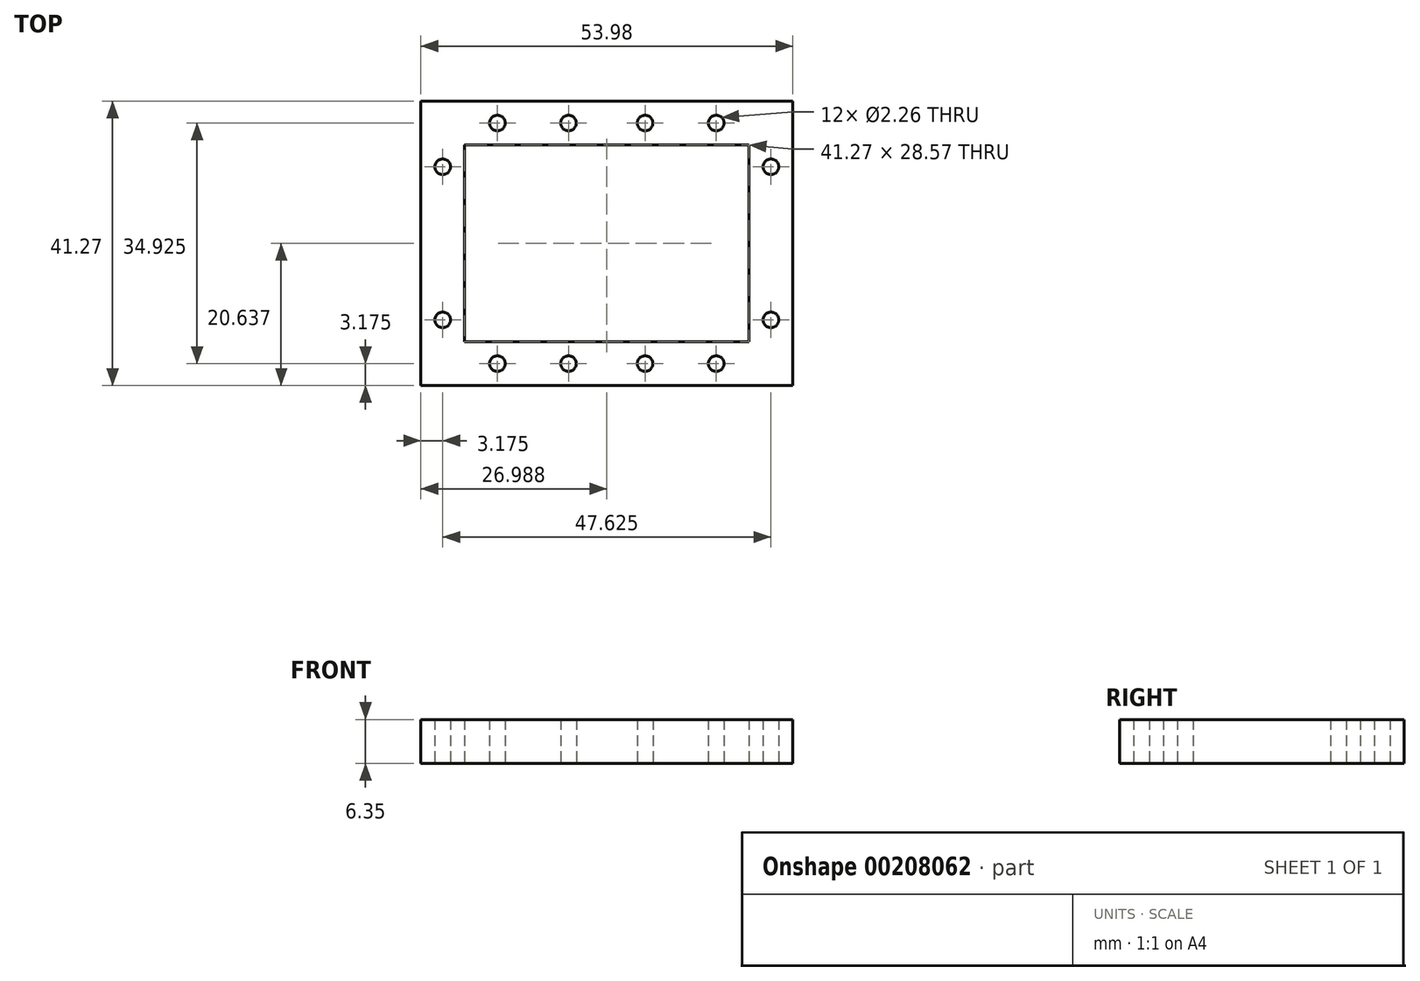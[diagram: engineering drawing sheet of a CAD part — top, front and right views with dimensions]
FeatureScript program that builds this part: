
annotation { "Feature Type Name" : "Feature", "Feature Type Description" : "" }
export const myFeature = defineFeature(function(context is Context, id is Id, definition is map)
    precondition{}
    {
        {
            var Q0;
            Q0=qCreatedBy(makeId("Top.planeOp"),FACE);
            var sketch = newSketch(context, id + "F0", { "sketchPlane" : qUnion([Q0])});
            skLineSegment(sketch, "E0", {"start": v(0, 0) * mm, "end": v(53.98, 0) * mm});
            skLineSegment(sketch, "E1", {"start": v(53.98, 0) * mm, "end": v(53.98, 41.27) * mm});
            skLineSegment(sketch, "E2", {"start": v(53.97, 41.27) * mm, "end": v(0, 41.27) * mm});
            skLineSegment(sketch, "E3", {"start": v(0, 41.27) * mm, "end": v(0, 0) * mm});
            skPoint(sketch, "E4", {"position": v(26.99, 20.64) * mm});
            skPoint(sketch, "E5", {"position": v(11.11, 3.18) * mm});
            skPoint(sketch, "E6", {"position": v(21.43, 3.18) * mm});
            skPoint(sketch, "E7", {"position": v(32.54, 3.18) * mm});
            skPoint(sketch, "E8", {"position": v(42.86, 3.18) * mm});
            skLineSegment(sketch, "E9", {"start": v(11.11, 3.18) * mm, "end": v(0, 3.18) * mm});
            skLineSegment(sketch, "E10", {"start": v(42.86, 3.18) * mm, "end": v(53.98, 3.18) * mm});
            skLineSegment(sketch, "E11", {"start": v(11.11, 3.18) * mm, "end": v(21.43, 3.18) * mm});
            skLineSegment(sketch, "E12", {"start": v(42.86, 3.18) * mm, "end": v(32.54, 3.18) * mm});
            skPoint(sketch, "E13", {"position": v(11.11, 38.1) * mm});
            skPoint(sketch, "E14", {"position": v(21.43, 38.1) * mm});
            skPoint(sketch, "E15", {"position": v(32.54, 38.1) * mm});
            skPoint(sketch, "E16", {"position": v(42.86, 38.1) * mm});
            skLineSegment(sketch, "E17", {"start": v(11.11, 38.1) * mm, "end": v(0, 38.1) * mm});
            skLineSegment(sketch, "E18", {"start": v(42.86, 38.1) * mm, "end": v(53.97, 38.1) * mm});
            skLineSegment(sketch, "E19", {"start": v(11.11, 38.1) * mm, "end": v(21.43, 38.1) * mm});
            skLineSegment(sketch, "E20", {"start": v(42.86, 38.1) * mm, "end": v(32.54, 38.1) * mm});
            skPoint(sketch, "E21", {"position": v(3.18, 9.53) * mm});
            skPoint(sketch, "E22", {"position": v(3.18, 31.75) * mm});
            skLineSegment(sketch, "E23", {"start": v(3.18, 9.53) * mm, "end": v(3.18, 0) * mm});
            skLineSegment(sketch, "E24", {"start": v(3.18, 31.75) * mm, "end": v(3.18, 41.28) * mm});
            skPoint(sketch, "E25", {"position": v(50.8, 9.53) * mm});
            skPoint(sketch, "E26", {"position": v(50.8, 31.75) * mm});
            skLineSegment(sketch, "E27", {"start": v(50.8, 9.53) * mm, "end": v(50.8, 0) * mm});
            skLineSegment(sketch, "E28", {"start": v(50.8, 31.75) * mm, "end": v(50.8, 41.28) * mm});
            skSolve(sketch);
        }
        {
            var Q0;
            Q0 = qSketchRegion(id + "F0", true);
            extrude(context, id + "F1", {"entities" : qUnion([Q0]), "depth" : 6.35 * mm});
        }
        {
            var Q0;
            Q0=makeQuery(id+"F1.opExtrude","CAP_FACE",FACE,{"disambiguationData":[OSD([sQuery(id+"F0.wireOp",EDGE,"E0"),sQuery(id+"F0.wireOp",EDGE,"E1"),sQuery(id+"F0.wireOp",EDGE,"E2"),sQuery(id+"F0.wireOp",EDGE,"E3")])],"isStart":true});
            var sketch = newSketch(context, id + "F2", { "sketchPlane" : qUnion([Q0])});
            skLineSegment(sketch, "E29", {"start": v(6.35, -6.35) * mm, "end": v(47.62, -6.35) * mm});
            skLineSegment(sketch, "E30", {"start": v(47.62, -6.35) * mm, "end": v(47.62, -34.93) * mm});
            skLineSegment(sketch, "E31", {"start": v(47.62, -34.93) * mm, "end": v(6.35, -34.93) * mm});
            skLineSegment(sketch, "E32", {"start": v(6.35, -34.93) * mm, "end": v(6.35, -6.35) * mm});
            skPoint(sketch, "E33", {"position": v(26.99, -20.64) * mm});
            skSolve(sketch);
        }
        {
            var Q0;
            Q0 = qSketchRegion(id + "F2", true);
            extrude(context, id + "F3", {"entities" : qUnion([Q0]), "operationType" : NewBodyOperationType.REMOVE, "endBound" : BoundingType.UP_TO_NEXT, "oppositeDirection" : true, "depth" : 25.4 * mm});
        }
        {
            var Q0;
            Q0=sQuery(id+"F0.wireOp",VERTEX,"E5");
            var Q1;
            Q1=makeQuery(id+"F1.opExtrude","SWEPT_BODY",BODY,{"disambiguationData":[OSD([sQuery(id+"F0.wireOp",EDGE,"E0"),sQuery(id+"F0.wireOp",EDGE,"E1"),sQuery(id+"F0.wireOp",EDGE,"E2"),sQuery(id+"F0.wireOp",EDGE,"E3")])]});
            hole(context, id + "F4", {"style" : HoleStyle.SIMPLE, "endStyle" : HoleEndStyle.THROUGH, "oppositeDirection" : true, "standardTappedOrClearance" : lookupTablePath({ "standard" : "ANSI", "engagement" : "75%", "pitch" : "40 tpi", "size" : "#4", "type" : "Tapped" }), "standardBlindInLast" : lookupTablePath({ "standard" : "ANSI", "engagement" : "75%", "pitch" : "40 tpi", "size" : "#4", "type" : "Tapped" }), "holeDiameter" : 2.26 * mm, "showTappedDepth" : true, "tappedDepth" : 12.7 * mm, "tapClearance" : 3, "locations" : qUnion([Q0]), "scope" : qUnion([Q1]), "majorDiameter" : 2.84 * mm});
        }
        {
            var Q0;
            Q0=sQuery(id+"F0.wireOp",VERTEX,"E6");
            var Q1;
            Q1=makeQuery(id+"F1.opExtrude","SWEPT_BODY",BODY,{"disambiguationData":[OSD([sQuery(id+"F0.wireOp",EDGE,"E0"),sQuery(id+"F0.wireOp",EDGE,"E1"),sQuery(id+"F0.wireOp",EDGE,"E2"),sQuery(id+"F0.wireOp",EDGE,"E3")])]});
            hole(context, id + "F5", {"style" : HoleStyle.SIMPLE, "endStyle" : HoleEndStyle.THROUGH, "oppositeDirection" : true, "standardTappedOrClearance" : lookupTablePath({ "standard" : "ANSI", "engagement" : "75%", "pitch" : "40 tpi", "size" : "#4", "type" : "Tapped" }), "standardBlindInLast" : lookupTablePath({ "standard" : "ANSI", "engagement" : "75%", "pitch" : "40 tpi", "size" : "#4", "type" : "Tapped" }), "holeDiameter" : 2.26 * mm, "showTappedDepth" : true, "tappedDepth" : 12.7 * mm, "tapClearance" : 3, "locations" : qUnion([Q0]), "scope" : qUnion([Q1]), "majorDiameter" : 2.84 * mm});
        }
        {
            var Q0;
            Q0=sQuery(id+"F0.wireOp",VERTEX,"E7");
            var Q1;
            Q1=makeQuery(id+"F1.opExtrude","SWEPT_BODY",BODY,{"disambiguationData":[OSD([sQuery(id+"F0.wireOp",EDGE,"E0"),sQuery(id+"F0.wireOp",EDGE,"E1"),sQuery(id+"F0.wireOp",EDGE,"E2"),sQuery(id+"F0.wireOp",EDGE,"E3")])]});
            hole(context, id + "F6", {"style" : HoleStyle.SIMPLE, "endStyle" : HoleEndStyle.THROUGH, "oppositeDirection" : true, "standardTappedOrClearance" : lookupTablePath({ "standard" : "ANSI", "engagement" : "75%", "pitch" : "40 tpi", "size" : "#4", "type" : "Tapped" }), "standardBlindInLast" : lookupTablePath({ "standard" : "ANSI", "engagement" : "75%", "pitch" : "40 tpi", "size" : "#4", "type" : "Tapped" }), "holeDiameter" : 2.26 * mm, "showTappedDepth" : true, "tappedDepth" : 12.7 * mm, "tapClearance" : 3, "locations" : qUnion([Q0]), "scope" : qUnion([Q1]), "majorDiameter" : 2.84 * mm});
        }
        {
            var Q0;
            Q0=sQuery(id+"F0.wireOp",VERTEX,"E8");
            var Q1;
            Q1=makeQuery(id+"F1.opExtrude","SWEPT_BODY",BODY,{"disambiguationData":[OSD([sQuery(id+"F0.wireOp",EDGE,"E0"),sQuery(id+"F0.wireOp",EDGE,"E1"),sQuery(id+"F0.wireOp",EDGE,"E2"),sQuery(id+"F0.wireOp",EDGE,"E3")])]});
            hole(context, id + "F7", {"style" : HoleStyle.SIMPLE, "endStyle" : HoleEndStyle.THROUGH, "oppositeDirection" : true, "standardTappedOrClearance" : lookupTablePath({ "standard" : "ANSI", "engagement" : "75%", "pitch" : "40 tpi", "size" : "#4", "type" : "Tapped" }), "standardBlindInLast" : lookupTablePath({ "standard" : "ANSI", "engagement" : "75%", "pitch" : "40 tpi", "size" : "#4", "type" : "Tapped" }), "holeDiameter" : 2.26 * mm, "showTappedDepth" : true, "tappedDepth" : 12.7 * mm, "tapClearance" : 3, "locations" : qUnion([Q0]), "scope" : qUnion([Q1]), "majorDiameter" : 2.84 * mm});
        }
        {
            var Q0;
            Q0=sQuery(id+"F0.wireOp",VERTEX,"E13");
            var Q1;
            Q1=makeQuery(id+"F1.opExtrude","SWEPT_BODY",BODY,{"disambiguationData":[OSD([sQuery(id+"F0.wireOp",EDGE,"E0"),sQuery(id+"F0.wireOp",EDGE,"E1"),sQuery(id+"F0.wireOp",EDGE,"E2"),sQuery(id+"F0.wireOp",EDGE,"E3")])]});
            hole(context, id + "F8", {"style" : HoleStyle.SIMPLE, "endStyle" : HoleEndStyle.THROUGH, "oppositeDirection" : true, "standardTappedOrClearance" : lookupTablePath({ "standard" : "ANSI", "engagement" : "75%", "pitch" : "40 tpi", "size" : "#4", "type" : "Tapped" }), "standardBlindInLast" : lookupTablePath({ "standard" : "ANSI", "engagement" : "75%", "pitch" : "40 tpi", "size" : "#4", "type" : "Tapped" }), "holeDiameter" : 2.26 * mm, "showTappedDepth" : true, "tappedDepth" : 12.7 * mm, "tapClearance" : 3, "locations" : qUnion([Q0]), "scope" : qUnion([Q1]), "majorDiameter" : 2.84 * mm});
        }
        {
            var Q0;
            Q0=sQuery(id+"F0.wireOp",VERTEX,"E14");
            var Q1;
            Q1=makeQuery(id+"F1.opExtrude","SWEPT_BODY",BODY,{"disambiguationData":[OSD([sQuery(id+"F0.wireOp",EDGE,"E0"),sQuery(id+"F0.wireOp",EDGE,"E1"),sQuery(id+"F0.wireOp",EDGE,"E2"),sQuery(id+"F0.wireOp",EDGE,"E3")])]});
            hole(context, id + "F9", {"style" : HoleStyle.SIMPLE, "endStyle" : HoleEndStyle.THROUGH, "oppositeDirection" : true, "standardTappedOrClearance" : lookupTablePath({ "standard" : "ANSI", "engagement" : "75%", "pitch" : "40 tpi", "size" : "#4", "type" : "Tapped" }), "standardBlindInLast" : lookupTablePath({ "standard" : "ANSI", "engagement" : "75%", "pitch" : "40 tpi", "size" : "#4", "type" : "Tapped" }), "holeDiameter" : 2.26 * mm, "showTappedDepth" : true, "tappedDepth" : 12.7 * mm, "tapClearance" : 3, "locations" : qUnion([Q0]), "scope" : qUnion([Q1]), "majorDiameter" : 2.84 * mm});
        }
        {
            var Q0;
            Q0=sQuery(id+"F0.wireOp",VERTEX,"E15");
            var Q1;
            Q1=makeQuery(id+"F1.opExtrude","SWEPT_BODY",BODY,{"disambiguationData":[OSD([sQuery(id+"F0.wireOp",EDGE,"E0"),sQuery(id+"F0.wireOp",EDGE,"E1"),sQuery(id+"F0.wireOp",EDGE,"E2"),sQuery(id+"F0.wireOp",EDGE,"E3")])]});
            hole(context, id + "F10", {"style" : HoleStyle.SIMPLE, "endStyle" : HoleEndStyle.THROUGH, "oppositeDirection" : true, "standardTappedOrClearance" : lookupTablePath({ "standard" : "ANSI", "engagement" : "75%", "pitch" : "40 tpi", "size" : "#4", "type" : "Tapped" }), "standardBlindInLast" : lookupTablePath({ "standard" : "ANSI", "engagement" : "75%", "pitch" : "40 tpi", "size" : "#4", "type" : "Tapped" }), "holeDiameter" : 2.26 * mm, "showTappedDepth" : true, "tappedDepth" : 12.7 * mm, "tapClearance" : 3, "locations" : qUnion([Q0]), "scope" : qUnion([Q1]), "majorDiameter" : 2.84 * mm});
        }
        {
            var Q0;
            Q0=sQuery(id+"F0.wireOp",VERTEX,"E16");
            var Q1;
            Q1=makeQuery(id+"F1.opExtrude","SWEPT_BODY",BODY,{"disambiguationData":[OSD([sQuery(id+"F0.wireOp",EDGE,"E0"),sQuery(id+"F0.wireOp",EDGE,"E1"),sQuery(id+"F0.wireOp",EDGE,"E2"),sQuery(id+"F0.wireOp",EDGE,"E3")])]});
            hole(context, id + "F11", {"style" : HoleStyle.SIMPLE, "endStyle" : HoleEndStyle.THROUGH, "oppositeDirection" : true, "standardTappedOrClearance" : lookupTablePath({ "standard" : "ANSI", "engagement" : "75%", "pitch" : "40 tpi", "size" : "#4", "type" : "Tapped" }), "standardBlindInLast" : lookupTablePath({ "standard" : "ANSI", "engagement" : "75%", "pitch" : "40 tpi", "size" : "#4", "type" : "Tapped" }), "holeDiameter" : 2.26 * mm, "showTappedDepth" : true, "tappedDepth" : 12.7 * mm, "tapClearance" : 3, "locations" : qUnion([Q0]), "scope" : qUnion([Q1]), "majorDiameter" : 2.84 * mm});
        }
        {
            var Q0;
            Q0=sQuery(id+"F0.wireOp",VERTEX,"E21");
            var Q1;
            Q1=makeQuery(id+"F1.opExtrude","SWEPT_BODY",BODY,{"disambiguationData":[OSD([sQuery(id+"F0.wireOp",EDGE,"E0"),sQuery(id+"F0.wireOp",EDGE,"E1"),sQuery(id+"F0.wireOp",EDGE,"E2"),sQuery(id+"F0.wireOp",EDGE,"E3")])]});
            hole(context, id + "F12", {"style" : HoleStyle.SIMPLE, "endStyle" : HoleEndStyle.THROUGH, "oppositeDirection" : true, "standardTappedOrClearance" : lookupTablePath({ "standard" : "ANSI", "engagement" : "75%", "pitch" : "40 tpi", "size" : "#4", "type" : "Tapped" }), "standardBlindInLast" : lookupTablePath({ "standard" : "ANSI", "engagement" : "75%", "pitch" : "40 tpi", "size" : "#4", "type" : "Tapped" }), "holeDiameter" : 2.26 * mm, "showTappedDepth" : true, "tappedDepth" : 12.7 * mm, "tapClearance" : 3, "locations" : qUnion([Q0]), "scope" : qUnion([Q1]), "majorDiameter" : 2.84 * mm});
        }
        {
            var Q0;
            Q0=sQuery(id+"F0.wireOp",VERTEX,"E22");
            var Q1;
            Q1=makeQuery(id+"F1.opExtrude","SWEPT_BODY",BODY,{"disambiguationData":[OSD([sQuery(id+"F0.wireOp",EDGE,"E0"),sQuery(id+"F0.wireOp",EDGE,"E1"),sQuery(id+"F0.wireOp",EDGE,"E2"),sQuery(id+"F0.wireOp",EDGE,"E3")])]});
            hole(context, id + "F13", {"style" : HoleStyle.SIMPLE, "endStyle" : HoleEndStyle.THROUGH, "oppositeDirection" : true, "standardTappedOrClearance" : lookupTablePath({ "standard" : "ANSI", "engagement" : "75%", "pitch" : "40 tpi", "size" : "#4", "type" : "Tapped" }), "standardBlindInLast" : lookupTablePath({ "standard" : "ANSI", "engagement" : "75%", "pitch" : "40 tpi", "size" : "#4", "type" : "Tapped" }), "holeDiameter" : 2.26 * mm, "showTappedDepth" : true, "tappedDepth" : 12.7 * mm, "tapClearance" : 3, "locations" : qUnion([Q0]), "scope" : qUnion([Q1]), "majorDiameter" : 2.84 * mm});
        }
        {
            var Q0;
            Q0=sQuery(id+"F0.wireOp",VERTEX,"E25");
            var Q1;
            Q1=makeQuery(id+"F1.opExtrude","SWEPT_BODY",BODY,{"disambiguationData":[OSD([sQuery(id+"F0.wireOp",EDGE,"E0"),sQuery(id+"F0.wireOp",EDGE,"E1"),sQuery(id+"F0.wireOp",EDGE,"E2"),sQuery(id+"F0.wireOp",EDGE,"E3")])]});
            hole(context, id + "F14", {"style" : HoleStyle.SIMPLE, "endStyle" : HoleEndStyle.THROUGH, "oppositeDirection" : true, "standardTappedOrClearance" : lookupTablePath({ "standard" : "ANSI", "engagement" : "75%", "pitch" : "40 tpi", "size" : "#4", "type" : "Tapped" }), "standardBlindInLast" : lookupTablePath({ "standard" : "ANSI", "engagement" : "75%", "pitch" : "40 tpi", "size" : "#4", "type" : "Tapped" }), "holeDiameter" : 2.26 * mm, "showTappedDepth" : true, "tappedDepth" : 12.7 * mm, "tapClearance" : 3, "locations" : qUnion([Q0]), "scope" : qUnion([Q1]), "majorDiameter" : 2.84 * mm});
        }
        {
            var Q0;
            Q0=sQuery(id+"F0.wireOp",VERTEX,"E26");
            var Q1;
            Q1=makeQuery(id+"F1.opExtrude","SWEPT_BODY",BODY,{"disambiguationData":[OSD([sQuery(id+"F0.wireOp",EDGE,"E0"),sQuery(id+"F0.wireOp",EDGE,"E1"),sQuery(id+"F0.wireOp",EDGE,"E2"),sQuery(id+"F0.wireOp",EDGE,"E3")])]});
            hole(context, id + "F15", {"style" : HoleStyle.SIMPLE, "endStyle" : HoleEndStyle.THROUGH, "oppositeDirection" : true, "standardTappedOrClearance" : lookupTablePath({ "standard" : "ANSI", "engagement" : "75%", "pitch" : "40 tpi", "size" : "#4", "type" : "Tapped" }), "standardBlindInLast" : lookupTablePath({ "standard" : "ANSI", "engagement" : "75%", "pitch" : "40 tpi", "size" : "#4", "type" : "Tapped" }), "holeDiameter" : 2.26 * mm, "showTappedDepth" : true, "tappedDepth" : 12.7 * mm, "tapClearance" : 3, "locations" : qUnion([Q0]), "scope" : qUnion([Q1]), "majorDiameter" : 2.84 * mm});
        }
    });
